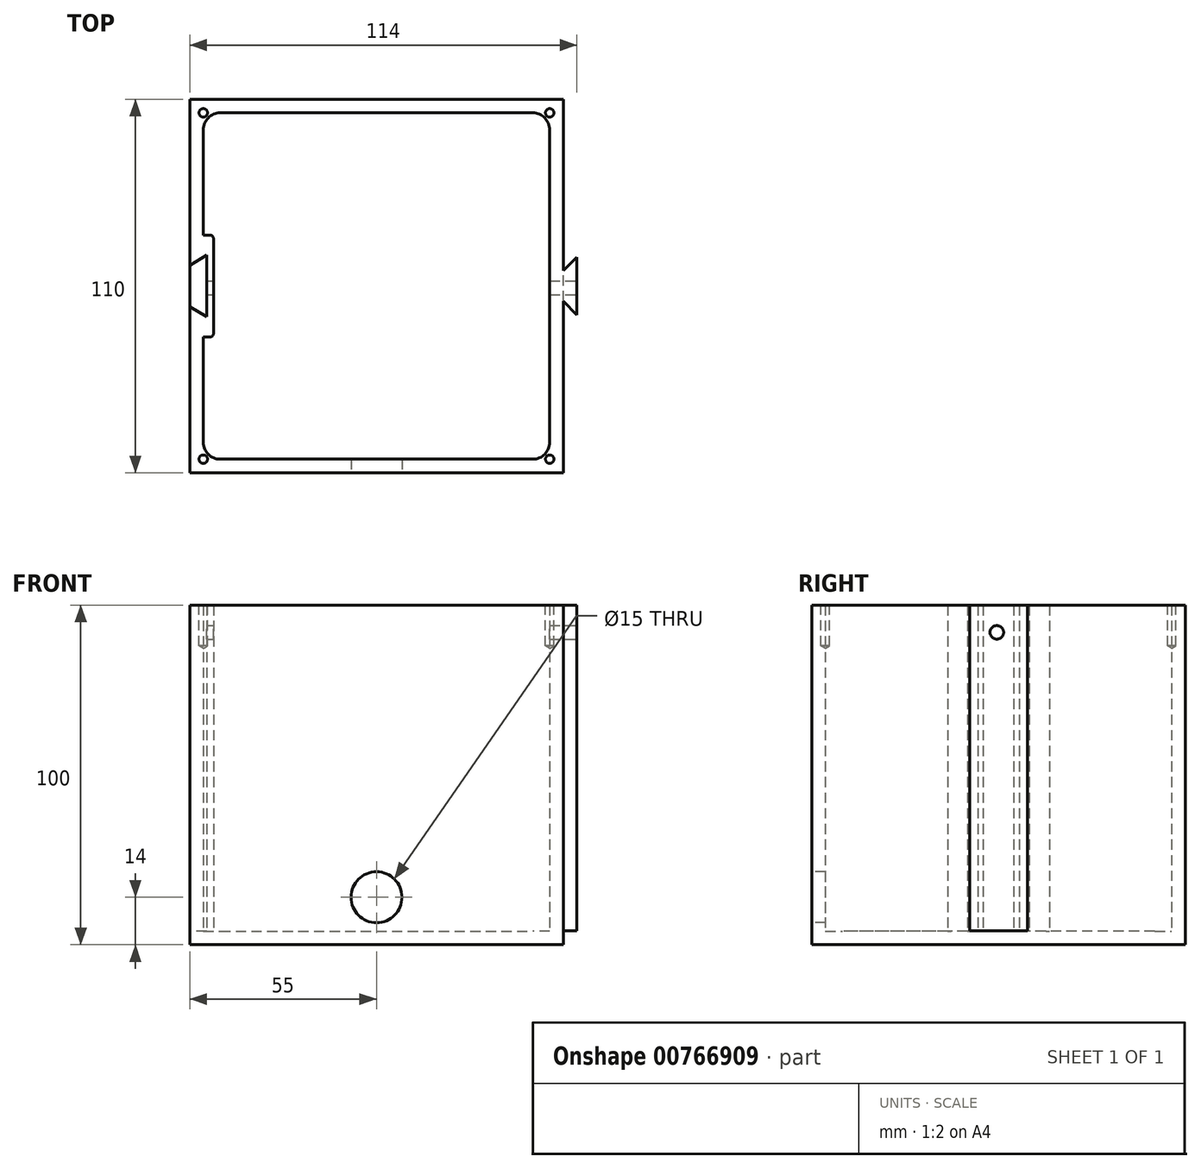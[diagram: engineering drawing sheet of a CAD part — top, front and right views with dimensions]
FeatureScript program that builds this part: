
annotation { "Feature Type Name" : "Feature", "Feature Type Description" : "" }
export const myFeature = defineFeature(function(context is Context, id is Id, definition is map)
    precondition{}
    {
        {
            var Q0;
            Q0=qCreatedBy(makeId("Top.planeOp"),FACE);
            var sketch = newSketch(context, id + "F0", { "sketchPlane" : qUnion([Q0])});
            skLineSegment(sketch, "E0.bottom", {"start": v(0, 0) * mm, "end": v(110, 0) * mm});
            skLineSegment(sketch, "E0.top", {"start": v(0, 110) * mm, "end": v(110, 110) * mm});
            skLineSegment(sketch, "E0.left", {"start": v(0, 0) * mm, "end": v(0, 48.93) * mm});
            skLineSegment(sketch, "E0.right", {"start": v(110, 0) * mm, "end": v(110, 50.5) * mm});
            skLineSegment(sketch, "E1.bottom", {"start": v(9, 106) * mm, "end": v(101, 106) * mm});
            skLineSegment(sketch, "E1.top", {"start": v(9, 4) * mm, "end": v(101, 4) * mm});
            skLineSegment(sketch, "E1.left", {"start": v(4, 101) * mm, "end": v(4, 70) * mm});
            skLineSegment(sketch, "E1.right", {"start": v(106, 101) * mm, "end": v(106, 9) * mm});
            skLineSegment(sketch, "E2", {"start": v(110, 59.5) * mm, "end": v(114, 63.5) * mm});
            skLineSegment(sketch, "E3", {"start": v(114, 63.5) * mm, "end": v(114, 46.5) * mm});
            skLineSegment(sketch, "E4", {"start": v(114, 46.5) * mm, "end": v(110, 50.5) * mm});
            skLineSegment(sketch, "E5.trimOffspring", {"start": v(110, 59.5) * mm, "end": v(110, 110) * mm});
            skLineSegment(sketch, "E6", {"start": v(5, 64.08) * mm, "end": v(0, 61.08) * mm});
            skLineSegment(sketch, "E7", {"start": v(5, 45.93) * mm, "end": v(0, 48.93) * mm});
            skLineSegment(sketch, "E8.trimOffspring", {"start": v(4, 40) * mm, "end": v(4, 9) * mm});
            skLineSegment(sketch, "E9.trimOffspring", {"start": v(0, 61.08) * mm, "end": v(0, 110) * mm});
            skPoint(sketch, "E10.visualSharp", {"position": v(4, 106) * mm});
            skArc(sketch, "E10.filletArc", {"start": v(9, 106) * mm, "mid": v(5.46, 104.54) * mm, "end": v(4, 101) * mm});
            skPoint(sketch, "E11.visualSharp", {"position": v(106, 106) * mm});
            skArc(sketch, "E11.filletArc", {"start": v(106, 101) * mm, "mid": v(104.54, 104.54) * mm, "end": v(101, 106) * mm});
            skPoint(sketch, "E12.visualSharp", {"position": v(106, 4) * mm});
            skArc(sketch, "E12.filletArc", {"start": v(101, 4) * mm, "mid": v(104.54, 5.46) * mm, "end": v(106, 9) * mm});
            skPoint(sketch, "E13.visualSharp", {"position": v(4, 4) * mm});
            skArc(sketch, "E13.filletArc", {"start": v(4, 9) * mm, "mid": v(5.46, 5.46) * mm, "end": v(9, 4) * mm});
            skLineSegment(sketch, "E14.bottom", {"start": v(4, 70) * mm, "end": v(6, 70) * mm});
            skLineSegment(sketch, "E14.top", {"start": v(4, 40) * mm, "end": v(6, 40) * mm});
            skLineSegment(sketch, "E14.right", {"start": v(7, 69) * mm, "end": v(7, 41) * mm});
            skLineSegment(sketch, "E15", {"start": v(0, 48.93) * mm, "end": v(0, 61.08) * mm, "construction": true});
            skLineSegment(sketch, "E16", {"start": v(0, 55) * mm, "end": v(25, 55) * mm, "construction": true});
            skPoint(sketch, "E17.visualSharp", {"position": v(7, 70) * mm});
            skArc(sketch, "E17.filletArc", {"start": v(7, 69) * mm, "mid": v(6.7, 69.7) * mm, "end": v(6, 70) * mm});
            skPoint(sketch, "E18.visualSharp", {"position": v(7, 40) * mm});
            skArc(sketch, "E18.filletArc", {"start": v(6, 40) * mm, "mid": v(6.7, 40.3) * mm, "end": v(7, 41) * mm});
            skLineSegment(sketch, "E19", {"start": v(5, 64.08) * mm, "end": v(5, 45.93) * mm});
            skLineSegment(sketch, "E20", {"start": v(114, 55) * mm, "end": v(91, 55) * mm, "construction": true});
            skPoint(sketch, "E20.endSnap0", {"position": v(106, 55) * mm});
            skSolve(sketch);
        }
        {
            var Q0;
            Q0=makeQuery(id+"F0.imprint","IMPRINT",FACE,{"disambiguationData":[TD([[makeQuery(id+"F0.imprint","IMPRINT",EDGE,{"derivedFrom":sQuery(id+"F0.wireOp",EDGE,"E0.bottom")}),1.0]])]});
            extrude(context, id + "F1", {"entities" : qUnion([Q0]), "depth" : 100 * mm, "offsetDistance" : 25 * mm});
        }
        {
            var Q0;
            Q0=qCreatedBy(makeId("Top.planeOp"),FACE);
            var sketch = newSketch(context, id + "F2", { "sketchPlane" : qUnion([Q0])});
            skLineSegment(sketch, "E21.bottom", {"start": v(0, 0) * mm, "end": v(110, 0) * mm});
            skLineSegment(sketch, "E21.top", {"start": v(0, 110) * mm, "end": v(110, 110) * mm});
            skLineSegment(sketch, "E21.left", {"start": v(0, 0) * mm, "end": v(0, 110) * mm});
            skLineSegment(sketch, "E21.right", {"start": v(110, 0) * mm, "end": v(110, 110) * mm});
            skSolve(sketch);
        }
        {
            var Q0;
            Q0=makeQuery(id+"F2.imprint","IMPRINT",FACE,{"disambiguationData":[TD([[makeQuery(id+"F2.imprint","IMPRINT",EDGE,{"derivedFrom":sQuery(id+"F2.wireOp",EDGE,"E21.bottom")}),1.0]])]});
            extrude(context, id + "F3", {"entities" : qUnion([Q0]), "operationType" : NewBodyOperationType.ADD, "depth" : 4 * mm, "offsetDistance" : 25 * mm});
        }
        {
            var Q0;
            Q0=makeQuery(id+"F1.opExtrude","SWEPT_FACE",FACE,{"disambiguationData":[OSD([sQuery(id+"F0.wireOp",EDGE,"E3")])]});
            var sketch = newSketch(context, id + "F4", { "sketchPlane" : qUnion([Q0])});
            skLineSegment(sketch, "E22.bottom", {"start": v(0, 0) * mm, "end": v(110, 0) * mm});
            skLineSegment(sketch, "E22.top", {"start": v(0, 4.05) * mm, "end": v(110, 4.05) * mm});
            skLineSegment(sketch, "E22.left", {"start": v(0, 0) * mm, "end": v(0, 4.05) * mm});
            skLineSegment(sketch, "E22.right", {"start": v(110, 0) * mm, "end": v(110, 4.05) * mm});
            skSolve(sketch);
        }
        {
            var Q0;
            {var subQ0=sQuery(id+"F4.wireOp",EDGE,"E22.bottom");var subQ1=sQuery(id+"F0.wireOp",EDGE,"E3");var subQ2=makeQuery(id+"F1.opExtrude","SWEPT_EDGE",EDGE,{"disambiguationData":[OSD([sQuery(id+"F0.wireOp",EDGE,"E2"),subQ1])]});var subQ3=makeQuery(id+"F4.imprint","INTERSECT",VERTEX,{"derivedFrom":[subQ2,subQ0]});var subQ4=makeQuery(id+"F1.opExtrude","SWEPT_EDGE",EDGE,{"disambiguationData":[OSD([subQ1,sQuery(id+"F0.wireOp",EDGE,"E4")])]});var subQ5=makeQuery(id+"F4.imprint","INTERSECT",VERTEX,{"derivedFrom":[subQ4,subQ0]});Q0=makeQuery(id+"F4.imprint","IMPRINT",FACE,{"disambiguationData":[TD([[makeQuery(id+"F4.imprint","IMPRINT",EDGE,{"disambiguationData":[TD([[subQ3,-1.0],[subQ5,1.0]])],"derivedFrom":subQ0}),-1.0]])]});}
            extrude(context, id + "F5", {"entities" : qUnion([Q0]), "operationType" : NewBodyOperationType.REMOVE, "oppositeDirection" : true, "depth" : 4 * mm, "offsetDistance" : 25 * mm});
        }
        {
            var Q0;
            Q0=makeQuery(id+"F1.opExtrude","SWEPT_FACE",FACE,{"disambiguationData":[OSD([sQuery(id+"F0.wireOp",EDGE,"E3")])]});
            var sketch = newSketch(context, id + "F6", { "sketchPlane" : qUnion([Q0])});
            skPoint(sketch, "E23", {"position": v(54.5, 92) * mm});
            skSolve(sketch);
        }
        {
            var Q0;
            Q0=sQuery(id+"F6.wireOp",VERTEX,"E23");
            var Q1;
            Q1=makeQuery(id+"F1.opExtrude","SWEPT_BODY",BODY,{"disambiguationData":[OSD([sQuery(id+"F0.wireOp",EDGE,"E0.bottom"),sQuery(id+"F0.wireOp",EDGE,"E0.top"),sQuery(id+"F0.wireOp",EDGE,"E0.left"),sQuery(id+"F0.wireOp",EDGE,"E0.right"),sQuery(id+"F0.wireOp",EDGE,"E1.bottom"),sQuery(id+"F0.wireOp",EDGE,"E1.top"),sQuery(id+"F0.wireOp",EDGE,"E1.left"),sQuery(id+"F0.wireOp",EDGE,"E1.right"),sQuery(id+"F0.wireOp",EDGE,"E2"),sQuery(id+"F0.wireOp",EDGE,"E3"),sQuery(id+"F0.wireOp",EDGE,"E4"),sQuery(id+"F0.wireOp",EDGE,"E5.trimOffspring"),sQuery(id+"F0.wireOp",EDGE,"E6"),sQuery(id+"F0.wireOp",EDGE,"E7"),sQuery(id+"F0.wireOp",EDGE,"E8.trimOffspring"),sQuery(id+"F0.wireOp",EDGE,"E9.trimOffspring"),sQuery(id+"F0.wireOp",EDGE,"E10.filletArc"),sQuery(id+"F0.wireOp",EDGE,"E11.filletArc"),sQuery(id+"F0.wireOp",EDGE,"E12.filletArc"),sQuery(id+"F0.wireOp",EDGE,"E13.filletArc"),sQuery(id+"F0.wireOp",EDGE,"E14.bottom"),sQuery(id+"F0.wireOp",EDGE,"E14.top"),sQuery(id+"F0.wireOp",EDGE,"E14.left"),sQuery(id+"F0.wireOp",EDGE,"E14.right"),sQuery(id+"F0.wireOp",EDGE,"E17.filletArc"),sQuery(id+"F0.wireOp",EDGE,"E18.filletArc")])]});
            hole(context, id + "F7", {"style" : HoleStyle.SIMPLE, "endStyle" : HoleEndStyle.THROUGH, "holeDiameter" : 4 * mm, "majorDiameter" : 5 * mm, "isTappedThrough" : true, "tappedDepth" : 12 * mm, "tapClearance" : 3, "locations" : qUnion([Q0]), "scope" : qUnion([Q1])});
        }
        {
            var Q0;
            Q0=makeQuery(id+"F1.opExtrude","SWEPT_FACE",FACE,{"disambiguationData":[OSD([sQuery(id+"F0.wireOp",EDGE,"E0.bottom")])]});
            var sketch = newSketch(context, id + "F8", { "sketchPlane" : qUnion([Q0])});
            skCircle(sketch, "E24", {"center": v(55, 14) * mm, "radius": 7.5 * mm});
            skSolve(sketch);
        }
        {
            var Q0;
            Q0=makeQuery(id+"F8.imprint","IMPRINT",FACE,{"disambiguationData":[TD([[makeQuery(id+"F8.imprint","IMPRINT",EDGE,{"derivedFrom":sQuery(id+"F8.wireOp",EDGE,"E24")}),1.0]])]});
            extrude(context, id + "F9", {"entities" : qUnion([Q0]), "operationType" : NewBodyOperationType.REMOVE, "oppositeDirection" : true, "depth" : 25 * mm, "offsetDistance" : 25 * mm});
        }
        {
            var Q0;
            Q0=makeQuery(id+"F1.opExtrude","CAP_FACE",FACE,{"disambiguationData":[OSD([sQuery(id+"F0.wireOp",EDGE,"E0.bottom"),sQuery(id+"F0.wireOp",EDGE,"E0.top"),sQuery(id+"F0.wireOp",EDGE,"E0.left"),sQuery(id+"F0.wireOp",EDGE,"E0.right"),sQuery(id+"F0.wireOp",EDGE,"E1.bottom"),sQuery(id+"F0.wireOp",EDGE,"E1.top"),sQuery(id+"F0.wireOp",EDGE,"E1.left"),sQuery(id+"F0.wireOp",EDGE,"E1.right"),sQuery(id+"F0.wireOp",EDGE,"E2"),sQuery(id+"F0.wireOp",EDGE,"E3"),sQuery(id+"F0.wireOp",EDGE,"E4"),sQuery(id+"F0.wireOp",EDGE,"E5.trimOffspring"),sQuery(id+"F0.wireOp",EDGE,"E6"),sQuery(id+"F0.wireOp",EDGE,"E7"),sQuery(id+"F0.wireOp",EDGE,"E8.trimOffspring"),sQuery(id+"F0.wireOp",EDGE,"E9.trimOffspring"),sQuery(id+"F0.wireOp",EDGE,"E10.filletArc"),sQuery(id+"F0.wireOp",EDGE,"E11.filletArc"),sQuery(id+"F0.wireOp",EDGE,"E12.filletArc"),sQuery(id+"F0.wireOp",EDGE,"E13.filletArc"),sQuery(id+"F0.wireOp",EDGE,"E14.bottom"),sQuery(id+"F0.wireOp",EDGE,"E14.top"),sQuery(id+"F0.wireOp",EDGE,"E14.left"),sQuery(id+"F0.wireOp",EDGE,"E14.right"),sQuery(id+"F0.wireOp",EDGE,"E17.filletArc"),sQuery(id+"F0.wireOp",EDGE,"E18.filletArc")])],"isStart":false});
            var sketch = newSketch(context, id + "F10", { "sketchPlane" : qUnion([Q0])});
            skPoint(sketch, "E25", {"position": v(4, 4) * mm});
            skPoint(sketch, "E26", {"position": v(106, 4) * mm});
            skPoint(sketch, "E27", {"position": v(106, 106) * mm});
            skPoint(sketch, "E28", {"position": v(4, 106) * mm});
            skSolve(sketch);
        }
        {
            var Q0;
            Q0=sQuery(id+"F10.wireOp",VERTEX,"E28");
            var Q1;
            Q1=sQuery(id+"F10.wireOp",VERTEX,"E27");
            var Q2;
            Q2=sQuery(id+"F10.wireOp",VERTEX,"E26");
            var Q3;
            Q3=sQuery(id+"F10.wireOp",VERTEX,"E25");
            var Q4;
            Q4=makeQuery(id+"F1.opExtrude","SWEPT_BODY",BODY,{"disambiguationData":[OSD([sQuery(id+"F0.wireOp",EDGE,"E0.bottom"),sQuery(id+"F0.wireOp",EDGE,"E0.top"),sQuery(id+"F0.wireOp",EDGE,"E0.left"),sQuery(id+"F0.wireOp",EDGE,"E0.right"),sQuery(id+"F0.wireOp",EDGE,"E1.bottom"),sQuery(id+"F0.wireOp",EDGE,"E1.top"),sQuery(id+"F0.wireOp",EDGE,"E1.left"),sQuery(id+"F0.wireOp",EDGE,"E1.right"),sQuery(id+"F0.wireOp",EDGE,"E2"),sQuery(id+"F0.wireOp",EDGE,"E3"),sQuery(id+"F0.wireOp",EDGE,"E4"),sQuery(id+"F0.wireOp",EDGE,"E5.trimOffspring"),sQuery(id+"F0.wireOp",EDGE,"E6"),sQuery(id+"F0.wireOp",EDGE,"E7"),sQuery(id+"F0.wireOp",EDGE,"E8.trimOffspring"),sQuery(id+"F0.wireOp",EDGE,"E9.trimOffspring"),sQuery(id+"F0.wireOp",EDGE,"E10.filletArc"),sQuery(id+"F0.wireOp",EDGE,"E11.filletArc"),sQuery(id+"F0.wireOp",EDGE,"E12.filletArc"),sQuery(id+"F0.wireOp",EDGE,"E13.filletArc"),sQuery(id+"F0.wireOp",EDGE,"E14.bottom"),sQuery(id+"F0.wireOp",EDGE,"E14.top"),sQuery(id+"F0.wireOp",EDGE,"E14.left"),sQuery(id+"F0.wireOp",EDGE,"E14.right"),sQuery(id+"F0.wireOp",EDGE,"E17.filletArc"),sQuery(id+"F0.wireOp",EDGE,"E18.filletArc")])]});
            hole(context, id + "F11", {"style" : HoleStyle.SIMPLE, "endStyle" : HoleEndStyle.BLIND, "holeDiameter" : 2.5 * mm, "majorDiameter" : 5 * mm, "holeDepth" : 12 * mm, "isTappedThrough" : true, "tappedDepth" : 12 * mm, "tapClearance" : 3, "locations" : qUnion([Q0, Q1, Q2, Q3]), "scope" : qUnion([Q4])});
        }
    });
